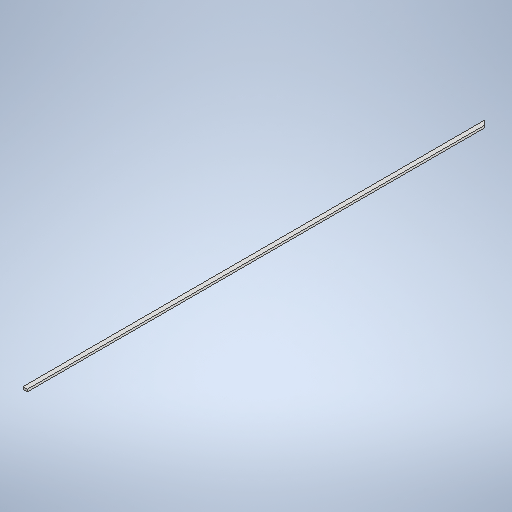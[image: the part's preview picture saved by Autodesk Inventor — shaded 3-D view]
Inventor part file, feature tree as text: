
AUTODESK INVENTOR PART (.ipt)
format: ipt  version: 2025.1 (Build 291241000, 241)  size: 270,848 bytes
history: native  units: mm
features: extrude x3, sketch x3, projected_geometry x1
ambient origin geometry x8: Origin, YZ Plane, XZ Plane, XY Plane, X Axis, Y Axis, Z Axis, Center Point
bodies: Solid1 (feature_tree)
feature tree (7):
  extrude  "Extrusion1"  Depth=2000.0mm
  extrude  "Extrusion2"  Depth=10.0mm TaperAngle=0.0deg
  extrude  "Extrusion3"  Depth=10.0mm
  sketch  "Sketch1"  dims[d0=19.0mm d1=2000.0mm]
  sketch  "Sketch2"  dims[d2=10.0mm d3=0.0mm d5=10.0mm d6=0.0mm]
  projected_geometry  "Projected Loop1"
  sketch  "Sketch3"  dims[d7=45.0deg d8=6.0mm d9=40.0mm d10=170.0mm d11=10.0mm d12=0.0mm]
